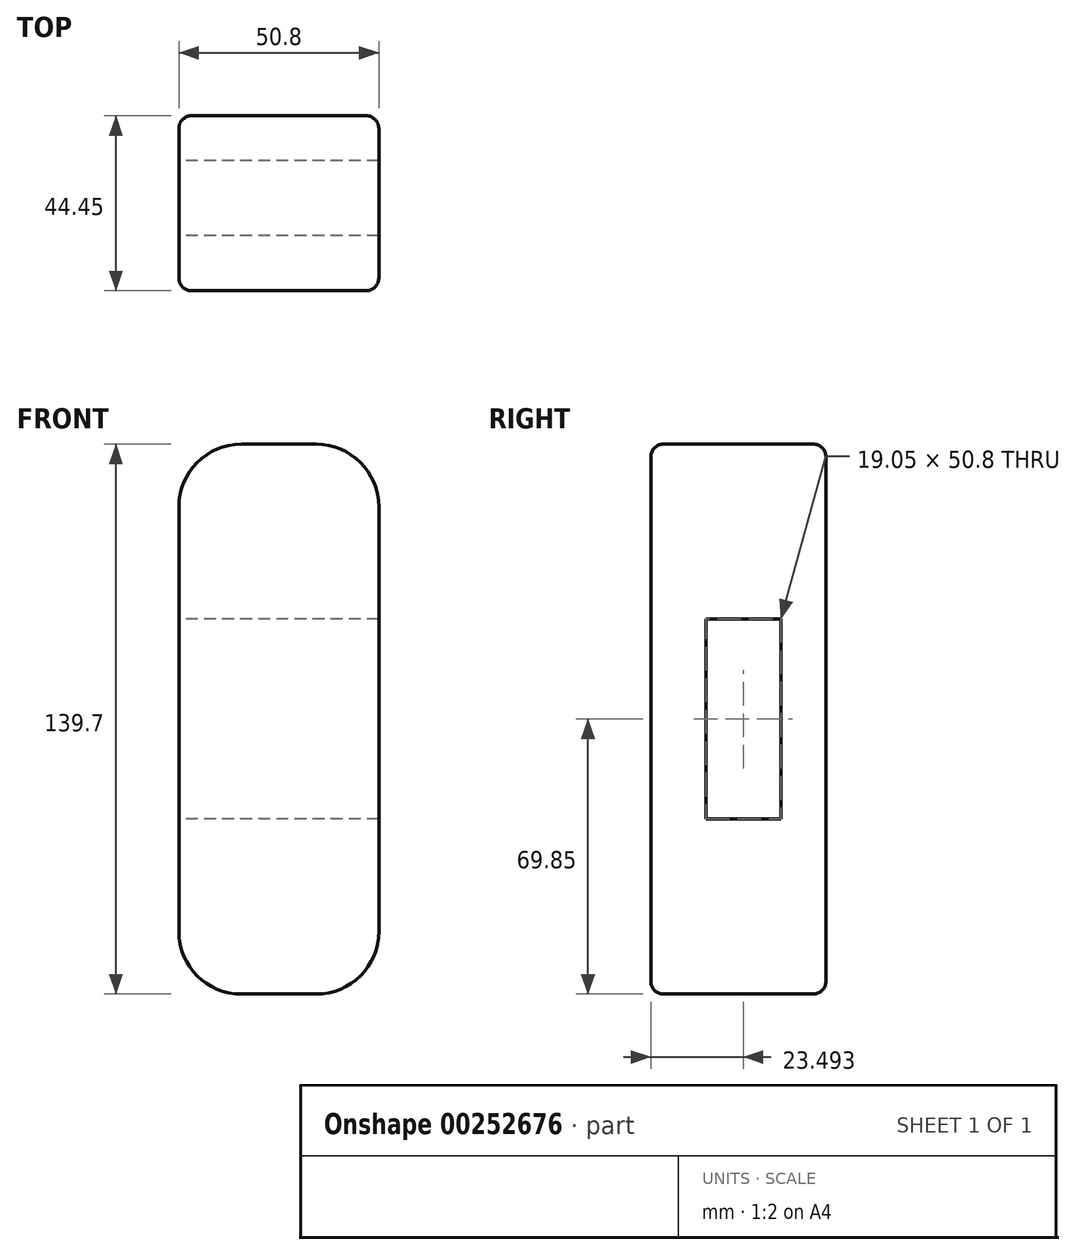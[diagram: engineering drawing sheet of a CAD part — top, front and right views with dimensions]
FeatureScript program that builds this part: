
annotation { "Feature Type Name" : "Feature", "Feature Type Description" : "" }
export const myFeature = defineFeature(function(context is Context, id is Id, definition is map)
    precondition{}
    {
        {
            var Q0;
            Q0=qCreatedBy(makeId("Front.planeOp"),FACE);
            var sketch = newSketch(context, id + "F0", { "sketchPlane" : qUnion([Q0])});
            skLineSegment(sketch, "E0.bottom", {"start": v(-9.52, 69.85) * mm, "end": v(9.53, 69.85) * mm});
            skLineSegment(sketch, "E0.top", {"start": v(-9.53, -69.85) * mm, "end": v(9.53, -69.85) * mm});
            skLineSegment(sketch, "E0.left", {"start": v(-25.4, 53.98) * mm, "end": v(-25.4, -53.98) * mm});
            skLineSegment(sketch, "E0.right", {"start": v(25.4, 53.97) * mm, "end": v(25.4, -53.98) * mm});
            skPoint(sketch, "E0.middle", {"position": v(0, 0) * mm});
            skPoint(sketch, "E1.visualSharp", {"position": v(-25.4, 69.85) * mm});
            skArc(sketch, "E1.filletArc", {"start": v(-9.52, 69.85) * mm, "mid": v(-20.75, 65.2) * mm, "end": v(-25.4, 53.98) * mm});
            skPoint(sketch, "E2.visualSharp", {"position": v(25.4, 69.85) * mm});
            skArc(sketch, "E2.filletArc", {"start": v(25.4, 53.97) * mm, "mid": v(20.75, 65.2) * mm, "end": v(9.53, 69.85) * mm});
            skPoint(sketch, "E3.visualSharp", {"position": v(25.4, -69.85) * mm});
            skArc(sketch, "E3.filletArc", {"start": v(9.53, -69.85) * mm, "mid": v(20.75, -65.2) * mm, "end": v(25.4, -53.98) * mm});
            skPoint(sketch, "E4.visualSharp", {"position": v(-25.4, -69.85) * mm});
            skArc(sketch, "E4.filletArc", {"start": v(-25.4, -53.98) * mm, "mid": v(-20.75, -65.2) * mm, "end": v(-9.53, -69.85) * mm});
            skSolve(sketch);
        }
        {
            var Q0;
            Q0=makeQuery(id+"F0.imprint","IMPRINT",FACE,{"disambiguationData":[TD([[makeQuery(id+"F0.imprint","IMPRINT",EDGE,{"derivedFrom":sQuery(id+"F0.wireOp",EDGE,"E0.bottom")}),-1.0]])]});
            extrude(context, id + "F1", {"entities" : qUnion([Q0]), "depth" : 44.45 * mm});
        }
        {
            var Q0;
            Q0=makeQuery(id+"F1.opExtrude","CAP_EDGE",EDGE,{"disambiguationData":[OSD([sQuery(id+"F0.wireOp",EDGE,"E0.left")])],"isStart":false});
            var Q1;
            Q1=makeQuery(id+"F1.opExtrude","CAP_EDGE",EDGE,{"disambiguationData":[OSD([sQuery(id+"F0.wireOp",EDGE,"E0.right")])],"isStart":true});
            fillet(context, id + "F2", {"entities" : qUnion([Q0, Q1]), "radius" : 3.17 * mm, "tangentPropagation" : true, "allowEdgeOverflow" : false});
        }
        {
            var Q0;
            Q0=qCreatedBy(makeId("Right.planeOp"),FACE);
            var sketch = newSketch(context, id + "F3", { "sketchPlane" : qUnion([Q0])});
            skLineSegment(sketch, "E5.bottom", {"start": v(-11.43, 25.4) * mm, "end": v(-30.48, 25.4) * mm});
            skLineSegment(sketch, "E5.top", {"start": v(-11.43, -25.4) * mm, "end": v(-30.48, -25.4) * mm});
            skLineSegment(sketch, "E5.left", {"start": v(-11.43, 25.4) * mm, "end": v(-11.43, -25.4) * mm});
            skLineSegment(sketch, "E5.right", {"start": v(-30.48, 25.4) * mm, "end": v(-30.48, -25.4) * mm});
            skPoint(sketch, "E5.middle", {"position": v(-20.96, 0) * mm});
            skSolve(sketch);
        }
        {
            var Q0;
            Q0 = qSketchRegion(id + "F3", true);
            extrude(context, id + "F4", {"entities" : qUnion([Q0]), "operationType" : NewBodyOperationType.REMOVE, "endBound" : BoundingType.SYMMETRIC, "depth" : 254 * mm});
        }
    });
